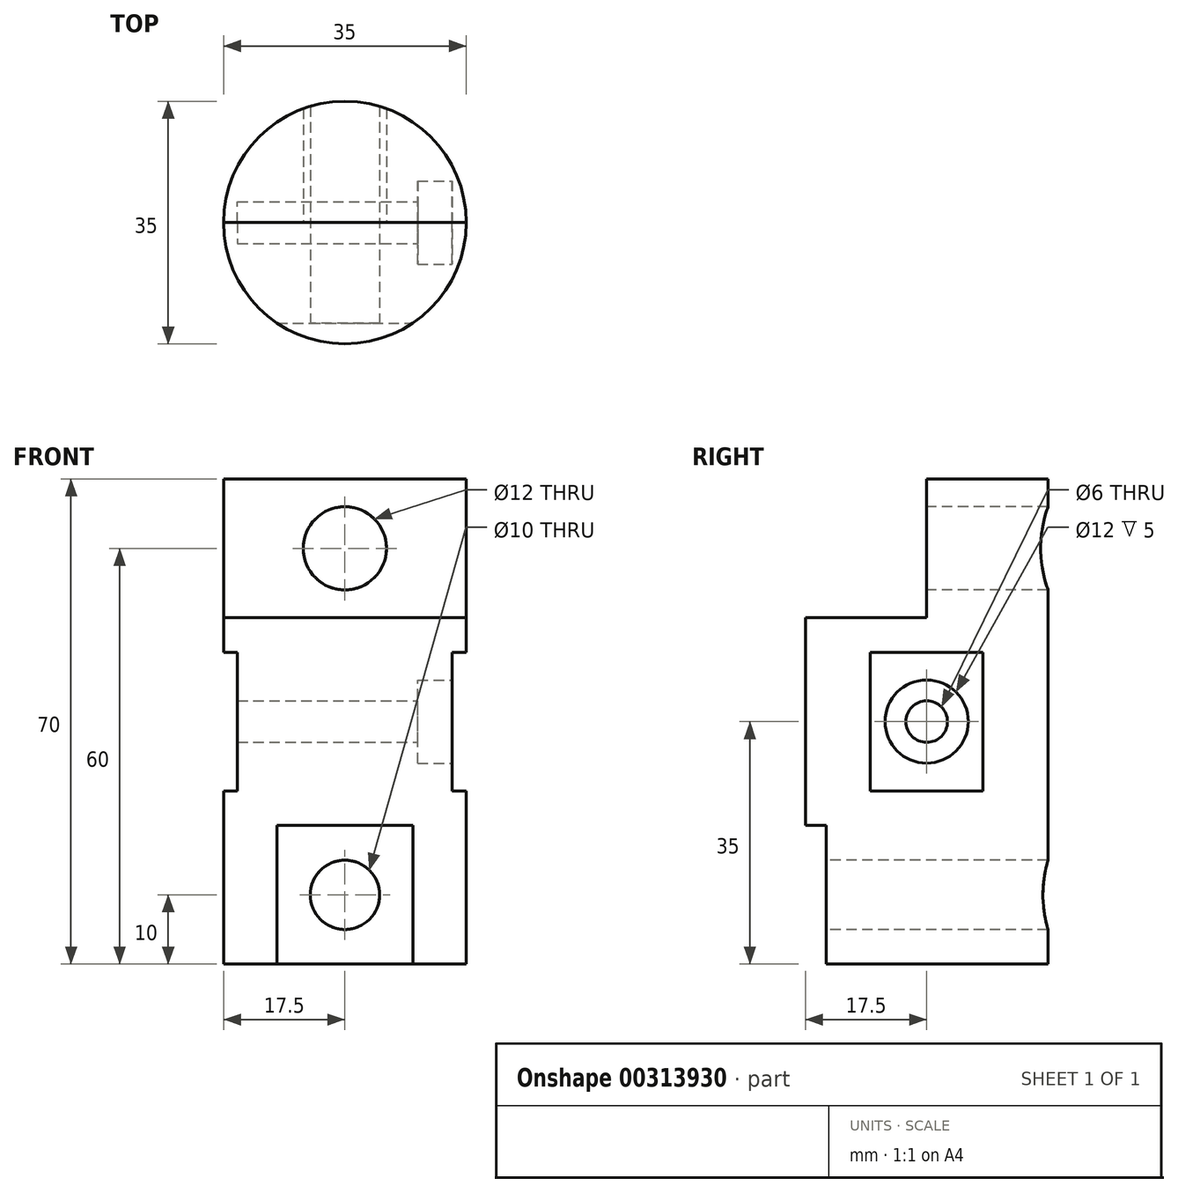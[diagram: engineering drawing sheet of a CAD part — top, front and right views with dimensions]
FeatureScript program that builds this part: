
annotation { "Feature Type Name" : "Feature", "Feature Type Description" : "" }
export const myFeature = defineFeature(function(context is Context, id is Id, definition is map)
    precondition{}
    {
        {
            var Q0;
            Q0=qCreatedBy(makeId("Front.planeOp"),FACE);
            var sketch = newSketch(context, id + "F0", { "sketchPlane" : qUnion([Q0])});
            skLineSegment(sketch, "E0", {"start": v(0, 0) * mm, "end": v(17.5, 0) * mm});
            skLineSegment(sketch, "E1", {"start": v(17.5, 0) * mm, "end": v(17.5, 70) * mm});
            skLineSegment(sketch, "E2", {"start": v(17.5, 70) * mm, "end": v(0, 70) * mm});
            skLineSegment(sketch, "E3", {"start": v(0, 70) * mm, "end": v(0, 0) * mm});
            skLineSegment(sketch, "E4.MirrorCS", {"start": v(-17.5, 0) * mm, "end": v(-17.5, 70) * mm, "construction": true});
            skLineSegment(sketch, "E5.MirrorCS", {"start": v(-17.5, 70) * mm, "end": v(0, 70) * mm, "construction": true});
            skLineSegment(sketch, "E6.MirrorCS", {"start": v(0, 0) * mm, "end": v(-17.5, 0) * mm, "construction": true});
            skSolve(sketch);
        }
        {
            var Q0;
            Q0=makeQuery(id+"F0.imprint","IMPRINT",FACE,{"disambiguationData":[TD([[makeQuery(id+"F0.imprint","IMPRINT",EDGE,{"derivedFrom":sQuery(id+"F0.wireOp",EDGE,"E0")}),1.0]])]});
            var Q1;
            Q1=sQuery(id+"F0.wireOp",EDGE,"E3");
            revolve(context, id + "F1", {"entities" : qUnion([Q0]), "axis" : qUnion([Q1]), "revolveType" : RevolveType.FULL});
        }
        {
            var Q0;
            Q0=qCreatedBy(makeId("Right.planeOp"),FACE);
            var sketch = newSketch(context, id + "F2", { "sketchPlane" : qUnion([Q0])});
            skLineSegment(sketch, "E7", {"start": v(-17.5, 50) * mm, "end": v(0, 50) * mm});
            skLineSegment(sketch, "E8", {"start": v(0, 50) * mm, "end": v(0, 70) * mm});
            skLineSegment(sketch, "E9", {"start": v(0, 70) * mm, "end": v(-17.5, 70) * mm});
            skLineSegment(sketch, "E10", {"start": v(-17.5, 70) * mm, "end": v(-17.5, 50) * mm});
            skLineSegment(sketch, "E11.0", {"start": v(-17.5, 70) * mm, "end": v(17.5, 70) * mm});
            skSolve(sketch);
        }
        {
            var Q0;
            Q0 = qSketchRegion(id + "F2", true);
            extrude(context, id + "F3", {"entities" : qUnion([Q0]), "operationType" : NewBodyOperationType.REMOVE, "endBound" : BoundingType.THROUGH_ALL, "oppositeDirection" : true, "depth" : 25 * mm, "hasSecondDirection" : true, "secondDirectionBound" : SecondDirectionBoundingType.THROUGH_ALL, "secondDirectionOppositeDirection" : false, "secondDirectionDepth" : 25 * mm});
        }
        {
            var Q0;
            Q0=makeQuery(id+"F3.boolean.opBoolean","COPY",FACE,{"derivedFrom":makeQuery(id+"F3.opExtrude","SWEPT_FACE",FACE,{"disambiguationData":[OSD([sQuery(id+"F2.wireOp",EDGE,"E8")])]})});
            var sketch = newSketch(context, id + "F4", { "sketchPlane" : qUnion([Q0])});
            skLineSegment(sketch, "E12", {"start": v(-17.5, 70) * mm, "end": v(17.5, 50) * mm});
            skLineSegment(sketch, "E13", {"start": v(0, 60) * mm, "end": v(17.5, 70) * mm});
            skSolve(sketch);
        }
        {
            var Q0;
            Q0=sQuery(id+"F4.wireOp",VERTEX,"E13.start");
            var Q1;
            Q1=makeQuery(id+"F1.opRevolve","SWEPT_BODY",BODY,{"disambiguationData":[OSD([sQuery(id+"F0.wireOp",EDGE,"E0"),sQuery(id+"F0.wireOp",EDGE,"E1"),sQuery(id+"F0.wireOp",EDGE,"E2"),sQuery(id+"F0.wireOp",EDGE,"E3")])]});
            hole(context, id + "F5", {"style" : HoleStyle.SIMPLE, "endStyle" : HoleEndStyle.THROUGH, "holeDiameter" : 12 * mm, "tappedDepth" : 12 * mm, "tapClearance" : 3, "locations" : qUnion([Q0]), "scope" : qUnion([Q1])});
        }
        {
            var Q0;
            Q0=qCreatedBy(makeId("Front.planeOp"),FACE);
            var sketch = newSketch(context, id + "F6", { "sketchPlane" : qUnion([Q0])});
            skLineSegment(sketch, "E14.0", {"start": v(-17.5, 0) * mm, "end": v(17.5, 0) * mm});
            skLineSegment(sketch, "E15", {"start": v(-17.5, 0) * mm, "end": v(-17.5, 20) * mm});
            skLineSegment(sketch, "E16", {"start": v(-17.5, 20) * mm, "end": v(17.5, 20) * mm});
            skLineSegment(sketch, "E17", {"start": v(17.5, 20) * mm, "end": v(17.5, 0) * mm});
            skSolve(sketch);
        }
        {
            var Q0;
            Q0 = qSketchRegion(id + "F6", true);
            extrude(context, id + "F7", {"entities" : qUnion([Q0]), "operationType" : NewBodyOperationType.REMOVE, "endBound" : BoundingType.THROUGH_ALL, "depth" : 25 * mm, "hasSecondDirection" : true, "secondDirectionOppositeDirection" : false, "secondDirectionDepth" : 14.5 * mm});
        }
        {
            var Q0;
            Q0=makeQuery(id+"F7.boolean.opBoolean","COPY",FACE,{"derivedFrom":makeQuery(id+"F7.opExtrude","CAP_FACE",FACE,{"disambiguationData":[OSD([sQuery(id+"F6.wireOp",EDGE,"E14.0"),sQuery(id+"F6.wireOp",EDGE,"E15"),sQuery(id+"F6.wireOp",EDGE,"E16"),sQuery(id+"F6.wireOp",EDGE,"E17")])],"isStart":true})});
            var sketch = newSketch(context, id + "F8", { "sketchPlane" : qUnion([Q0])});
            skLineSegment(sketch, "E18", {"start": v(-9.8, 0) * mm, "end": v(9.8, 20) * mm});
            skLineSegment(sketch, "E19", {"start": v(0, 10) * mm, "end": v(9.8, 0) * mm});
            skSolve(sketch);
        }
        {
            var Q0;
            Q0=sQuery(id+"F8.wireOp",VERTEX,"E19.start");
            var Q1;
            Q1=makeQuery(id+"F1.opRevolve","SWEPT_BODY",BODY,{"disambiguationData":[OSD([sQuery(id+"F0.wireOp",EDGE,"E0"),sQuery(id+"F0.wireOp",EDGE,"E1"),sQuery(id+"F0.wireOp",EDGE,"E2"),sQuery(id+"F0.wireOp",EDGE,"E3")])]});
            hole(context, id + "F9", {"style" : HoleStyle.SIMPLE, "endStyle" : HoleEndStyle.THROUGH, "holeDiameter" : 10 * mm, "tappedDepth" : 1000 * mm, "tapClearance" : 3, "locations" : qUnion([Q0]), "scope" : qUnion([Q1])});
        }
        {
            var Q0;
            Q0=qCreatedBy(makeId("Front.planeOp"),FACE);
            var sketch = newSketch(context, id + "F10", { "sketchPlane" : qUnion([Q0])});
            skLineSegment(sketch, "E20.bottom", {"start": v(-17.5, 45) * mm, "end": v(-15.5, 45) * mm});
            skLineSegment(sketch, "E20.top", {"start": v(-17.5, 25) * mm, "end": v(-15.5, 25) * mm});
            skLineSegment(sketch, "E20.left", {"start": v(-17.5, 45) * mm, "end": v(-17.5, 25) * mm});
            skLineSegment(sketch, "E20.right", {"start": v(-15.5, 45) * mm, "end": v(-15.5, 25) * mm});
            skLineSegment(sketch, "E21.MirrorCS", {"start": v(17.5, 45) * mm, "end": v(17.5, 25) * mm});
            skLineSegment(sketch, "E22.MirrorCS", {"start": v(17.5, 45) * mm, "end": v(15.5, 45) * mm});
            skLineSegment(sketch, "E23.MirrorCS", {"start": v(15.5, 45) * mm, "end": v(15.5, 25) * mm});
            skLineSegment(sketch, "E24.MirrorCS", {"start": v(17.5, 25) * mm, "end": v(15.5, 25) * mm});
            skLineSegment(sketch, "E25", {"start": v(-17.5, 0) * mm, "end": v(-17.5, 50) * mm});
            skLineSegment(sketch, "E26", {"start": v(-17.5, 50) * mm, "end": v(-17.5, 70) * mm});
            skLineSegment(sketch, "E27", {"start": v(17.5, 50) * mm, "end": v(17.5, 0) * mm});
            skLineSegment(sketch, "E28", {"start": v(17.5, 70) * mm, "end": v(17.5, 50) * mm});
            skSolve(sketch);
        }
        {
            var Q0;
            Q0 = qSketchRegion(id + "F10", true);
            extrude(context, id + "F11", {"entities" : qUnion([Q0]), "operationType" : NewBodyOperationType.REMOVE, "endBound" : BoundingType.THROUGH_ALL, "oppositeDirection" : true, "depth" : 25 * mm, "hasSecondDirection" : true, "secondDirectionBound" : SecondDirectionBoundingType.THROUGH_ALL, "secondDirectionOppositeDirection" : false, "secondDirectionDepth" : 25 * mm});
        }
        {
            var Q0;
            Q0=makeQuery(id+"F11.boolean.opBoolean","COPY",FACE,{"derivedFrom":makeQuery(id+"F11.opExtrude","SWEPT_FACE",FACE,{"disambiguationData":[OSD([sQuery(id+"F10.wireOp",EDGE,"E23.MirrorCS")])]})});
            var sketch = newSketch(context, id + "F12", { "sketchPlane" : qUnion([Q0])});
            skLineSegment(sketch, "E29", {"start": v(-8.12, 25) * mm, "end": v(8.12, 45) * mm});
            skLineSegment(sketch, "E30", {"start": v(0, 35) * mm, "end": v(8.12, 25) * mm});
            skSolve(sketch);
        }
        {
            var Q0;
            Q0=sQuery(id+"F12.wireOp",VERTEX,"E30.start");
            var Q1;
            Q1=makeQuery(id+"F1.opRevolve","SWEPT_BODY",BODY,{"disambiguationData":[OSD([sQuery(id+"F0.wireOp",EDGE,"E0"),sQuery(id+"F0.wireOp",EDGE,"E1"),sQuery(id+"F0.wireOp",EDGE,"E2"),sQuery(id+"F0.wireOp",EDGE,"E3")])]});
            hole(context, id + "F13", {"style" : HoleStyle.C_BORE, "endStyle" : HoleEndStyle.THROUGH, "holeDiameter" : 6 * mm, "cBoreDiameter" : 12 * mm, "cBoreDepth" : 5 * mm, "tappedDepth" : 1000 * mm, "tapClearance" : 3, "locations" : qUnion([Q0]), "scope" : qUnion([Q1])});
        }
    });
